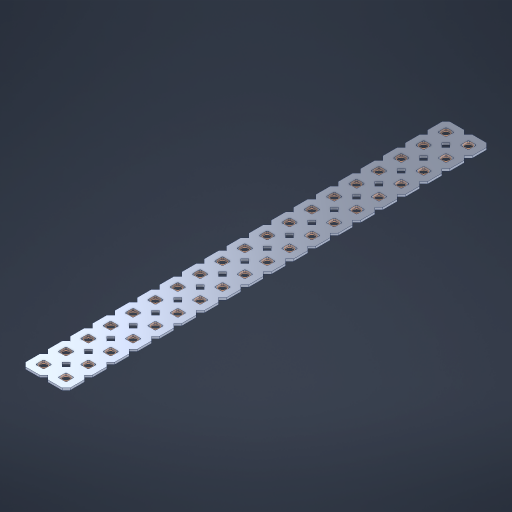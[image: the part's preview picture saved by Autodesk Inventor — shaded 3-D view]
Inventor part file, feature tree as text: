
AUTODESK INVENTOR PART (.ipt)
format: ipt  version: 2023 (Build 270158000, 158)  size: 693,248 bytes
history: native  units: in
note: dims shown in document units (in); Inventor stores cm internally (conversion verified against a paired STEP export)
features: other x39, extrude x37, sketch x2, pattern_linear x1
ambient origin geometry x8: Origin, YZ Plane, XZ Plane, XY Plane, X Axis, Y Axis, Z Axis, Center Point
bodies: Solid1 (feature_tree), Body (feature_tree)
feature tree (79):
  pattern_linear  "Rectangular Pattern1"  Spacing1=0.09in  [1 undecoded]
  sketch  "Sketch1"  dims[d1=0.5in]
  sketch  "Sketch2"  dims[d2=0.182in d3=0.09in d4=0.09in d5=0.09in d6=0.09in d7=0.09in d8=0.09in d9=0.09in d10=0.09in d11=0.02in d13=0.0in d14=0.172in d15=0.0625in d16=0.0in d19=0.5in d22=0.5in]
  other  "Srf1"
  other  "Srf126"
  other  "Srf127"
  other  "Srf128"
  other  "Srf129"
  other  "Srf130"
  other  "Srf131"
  other  "Srf250"
  other  "Srf251"
  other  "Srf252"
  other  "Srf253"
  other  "Srf254"
  other  "Srf255"
  other  "Srf256"
  other  "Srf257"
  other  "Srf258"
  other  "Srf259"
  other  "Srf260"
  other  "Srf261"
  other  "Srf268"
  other  "Srf269"
  other  "Srf270"
  other  "Srf271"
  other  "Srf272"
  other  "Srf273"
  other  "Srf274"
  other  "Srf275"
  other  "Srf276"
  other  "Srf277"
  other  "Srf278"
  other  "Srf279"
  other  "Srf280"
  other  "Srf281"
  other  "Srf282"
  other  "Srf283"
  other  "Srf284"
  other  "Srf285"
  other  "Srf286"
  other  "Circle"
  extrude  "ExtrusionSrf126"  Depth=0.09in
  extrude  "ExtrusionSrf127"  Depth=0.09in
  extrude  "ExtrusionSrf128"  Depth=0.09in
  extrude  "ExtrusionSrf129"  Depth=0.09in
  extrude  "ExtrusionSrf130"  Depth=0.09in
  extrude  "ExtrusionSrf131"  Depth=0.09in
  extrude  "ExtrusionSrf250"  Depth=0.09in
  extrude  "ExtrusionSrf251"  Depth=0.02in
  extrude  "ExtrusionSrf252"  TaperAngle=0.0deg  [1 undecoded]
  extrude  "ExtrusionSrf253"  Depth=0.5in
  extrude  "ExtrusionSrf254"  Depth=0.5in TaperAngle=0.0deg
  extrude  "ExtrusionSrf255"  Depth=0.5in
  extrude  "ExtrusionSrf256"  Depth=0.5in
  extrude  "ExtrusionSrf257"  [1 undecoded]
  extrude  "ExtrusionSrf258"  [1 undecoded]
  extrude  "ExtrusionSrf259"  [1 undecoded]
  extrude  "ExtrusionSrf260"  [1 undecoded]
  extrude  "ExtrusionSrf261"  [1 undecoded]
  extrude  "ExtrusionSrf268"  [1 undecoded]
  extrude  "ExtrusionSrf269"  [1 undecoded]
  extrude  "ExtrusionSrf270"  [1 undecoded]
  extrude  "ExtrusionSrf271"  [1 undecoded]
  extrude  "ExtrusionSrf272"  [1 undecoded]
  extrude  "ExtrusionSrf273"  [1 undecoded]
  extrude  "ExtrusionSrf274"  [1 undecoded]
  extrude  "ExtrusionSrf275"  [1 undecoded]
  extrude  "ExtrusionSrf276"  [1 undecoded]
  extrude  "ExtrusionSrf277"  [1 undecoded]
  extrude  "ExtrusionSrf278"  [1 undecoded]
  extrude  "ExtrusionSrf279"  [1 undecoded]
  extrude  "ExtrusionSrf280"  [1 undecoded]
  extrude  "ExtrusionSrf281"  [1 undecoded]
  extrude  "ExtrusionSrf282"  [1 undecoded]
  extrude  "ExtrusionSrf283"  [1 undecoded]
  extrude  "ExtrusionSrf284"  [1 undecoded]
  extrude  "ExtrusionSrf285"  [1 undecoded]
  extrude  "ExtrusionSrf286"  [1 undecoded]
note: 26 required parameter values undecoded (feature->parameter linkage not recoverable at this tier; creation-order binding heuristic only, values carry confidence <= 0.55)
